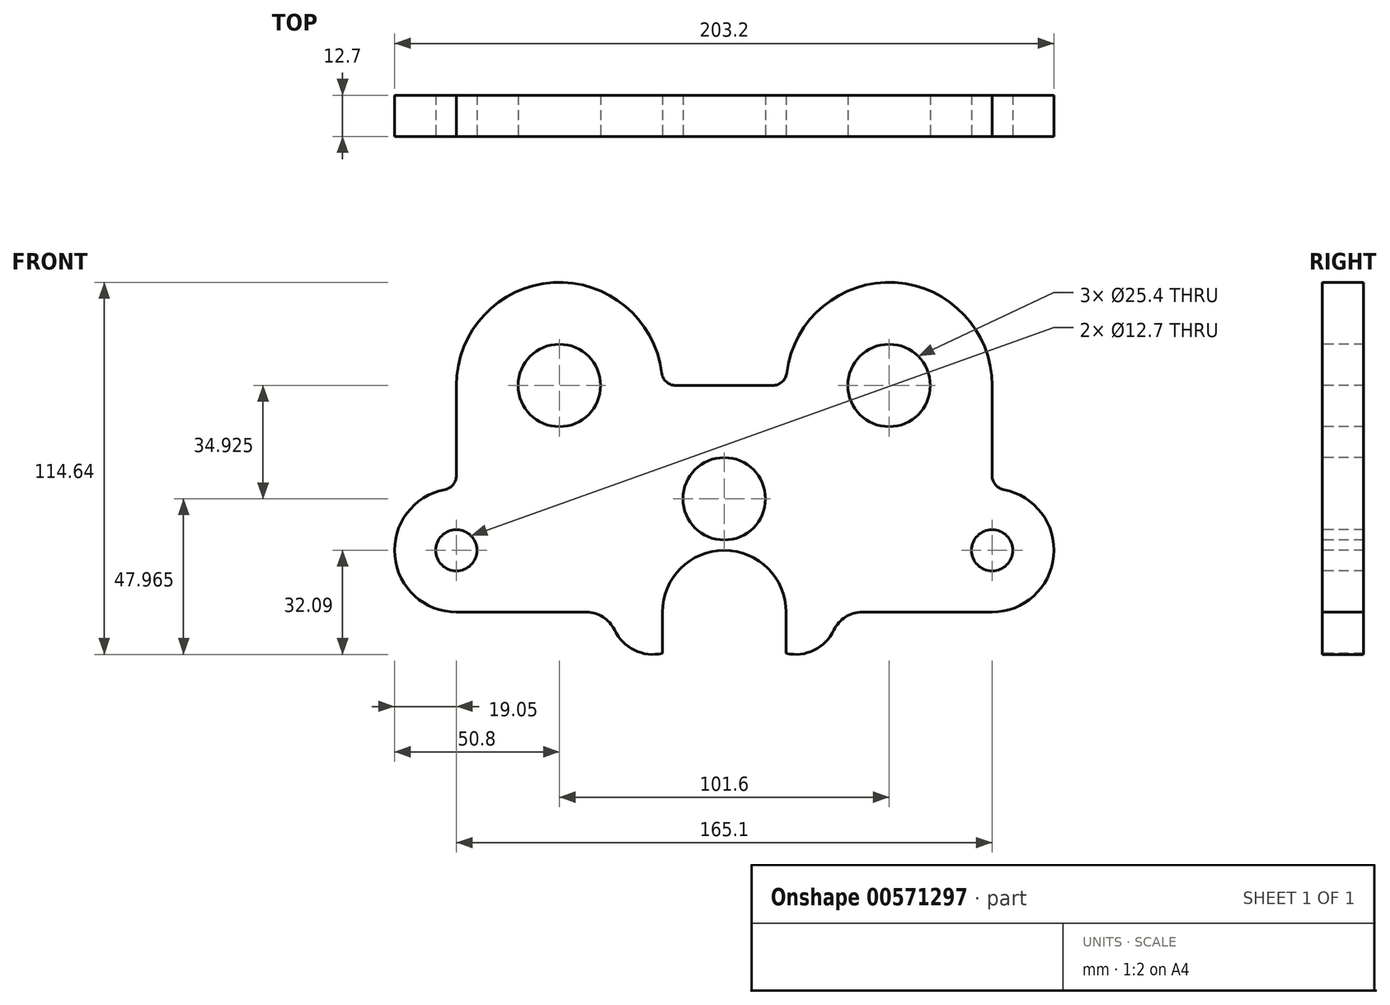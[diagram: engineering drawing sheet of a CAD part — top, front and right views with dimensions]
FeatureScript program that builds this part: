
annotation { "Feature Type Name" : "Feature", "Feature Type Description" : "" }
export const myFeature = defineFeature(function(context is Context, id is Id, definition is map)
    precondition{}
    {
        {
            var Q0;
            Q0=qCreatedBy(makeId("Front.planeOp"),FACE);
            var sketch = newSketch(context, id + "F0", { "sketchPlane" : qUnion([Q0])});
            skLineSegment(sketch, "E0", {"start": v(0, 97.1) * mm, "end": v(0, -60.42) * mm, "construction": true});
            skLineSegment(sketch, "E1", {"start": v(0, 69.85) * mm, "end": v(-14.9, 69.85) * mm});
            skArc(sketch, "E2", {"start": v(-19.29, 73.73) * mm, "mid": v(-52.74, 101.54) * mm, "end": v(-82.55, 69.85) * mm});
            skLineSegment(sketch, "E3", {"start": v(-82.55, 69.85) * mm, "end": v(-82.55, 42.1) * mm});
            skArc(sketch, "E4", {"start": v(-86.13, 37.76) * mm, "mid": v(-101.51, 17.25) * mm, "end": v(-82.55, 0) * mm});
            skLineSegment(sketch, "E5", {"start": v(-82.55, 0) * mm, "end": v(-42.46, 0) * mm});
            skArc(sketch, "E6", {"start": v(-42.46, 0) * mm, "mid": v(-37.34, -1.5) * mm, "end": v(-33.82, -5.5) * mm});
            skArc(sketch, "E7", {"start": v(-33.82, -5.5) * mm, "mid": v(-27.71, -11.72) * mm, "end": v(-19.05, -12.7) * mm});
            skLineSegment(sketch, "E8", {"start": v(-19.05, -12.7) * mm, "end": v(-19.05, 0) * mm});
            skLineSegment(sketch, "E9.MirrorCS", {"start": v(0, 69.85) * mm, "end": v(14.9, 69.85) * mm});
            skArc(sketch, "E10.MirrorCS", {"start": v(19.29, 73.73) * mm, "mid": v(52.74, 101.54) * mm, "end": v(82.55, 69.85) * mm});
            skLineSegment(sketch, "E11.MirrorCS", {"start": v(82.55, 69.85) * mm, "end": v(82.55, 42.1) * mm});
            skArc(sketch, "E12.MirrorCS", {"start": v(86.13, 37.76) * mm, "mid": v(101.51, 17.25) * mm, "end": v(82.55, 0) * mm});
            skLineSegment(sketch, "E13.MirrorCS", {"start": v(82.55, 0) * mm, "end": v(42.46, 0) * mm});
            skArc(sketch, "E14.MirrorCS", {"start": v(42.46, 0) * mm, "mid": v(37.34, -1.5) * mm, "end": v(33.82, -5.5) * mm});
            skArc(sketch, "E15.MirrorCS", {"start": v(33.82, -5.5) * mm, "mid": v(27.71, -11.72) * mm, "end": v(19.05, -12.7) * mm});
            skLineSegment(sketch, "E16.MirrorCS", {"start": v(19.05, -12.7) * mm, "end": v(19.05, 0) * mm});
            skCircle(sketch, "E17", {"center": v(50.8, 69.85) * mm, "radius": 12.7 * mm});
            skCircle(sketch, "E18", {"center": v(-82.55, 19.05) * mm, "radius": 6.35 * mm});
            skCircle(sketch, "E19", {"center": v(82.55, 19.05) * mm, "radius": 6.35 * mm});
            skCircle(sketch, "E20", {"center": v(-50.8, 69.85) * mm, "radius": 12.7 * mm});
            skArc(sketch, "E21", {"start": v(-19.05, 0) * mm, "mid": v(0, 19.05) * mm, "end": v(19.05, 0) * mm});
            skLineSegment(sketch, "E22", {"start": v(-50.8, 114.73) * mm, "end": v(-50.8, 41.14) * mm, "construction": true});
            skPoint(sketch, "E22.startSnap0", {"position": v(-50.8, 101.6) * mm});
            skLineSegment(sketch, "E23", {"start": v(-100.14, 69.85) * mm, "end": v(-29.1, 69.85) * mm, "construction": true});
            skLineSegment(sketch, "E24", {"start": v(-113.02, 19.05) * mm, "end": v(-60.7, 19.05) * mm, "construction": true});
            skPoint(sketch, "E24.endSnap0", {"position": v(-101.6, 19.05) * mm});
            skLineSegment(sketch, "E25", {"start": v(34.28, 69.85) * mm, "end": v(73, 69.85) * mm, "construction": true});
            skLineSegment(sketch, "E26", {"start": v(82.55, 33.07) * mm, "end": v(82.55, 5.84) * mm, "construction": true});
            skLineSegment(sketch, "E27", {"start": v(66.2, 19.05) * mm, "end": v(96.4, 19.05) * mm, "construction": true});
            skLineSegment(sketch, "E28", {"start": v(-23.99, 34.92) * mm, "end": v(20.1, 34.92) * mm, "construction": true});
            skCircle(sketch, "E29", {"center": v(0, 34.92) * mm, "radius": 12.7 * mm});
            skLineSegment(sketch, "E30", {"start": v(-31.9, 0) * mm, "end": v(42.46, 0) * mm, "construction": true});
            skPoint(sketch, "E31.visualSharp", {"position": v(-19.05, 69.85) * mm});
            skArc(sketch, "E31.filletArc", {"start": v(-19.29, 73.73) * mm, "mid": v(-17.83, 70.96) * mm, "end": v(-14.9, 69.85) * mm});
            skPoint(sketch, "E32.visualSharp", {"position": v(19.05, 69.85) * mm});
            skArc(sketch, "E32.filletArc", {"start": v(14.9, 69.85) * mm, "mid": v(17.83, 70.96) * mm, "end": v(19.29, 73.73) * mm});
            skPoint(sketch, "E33.visualSharp", {"position": v(-82.55, 38.1) * mm});
            skArc(sketch, "E33.filletArc", {"start": v(-86.13, 37.76) * mm, "mid": v(-83.56, 39.28) * mm, "end": v(-82.55, 42.1) * mm});
            skPoint(sketch, "E34.visualSharp", {"position": v(82.55, 38.1) * mm});
            skArc(sketch, "E34.filletArc", {"start": v(82.55, 42.1) * mm, "mid": v(83.56, 39.28) * mm, "end": v(86.13, 37.76) * mm});
            skSolve(sketch);
        }
        {
            var Q0;
            Q0 = qSketchRegion(id + "F0", true);
            extrude(context, id + "F1", {"entities" : qUnion([Q0]), "oppositeDirection" : true, "depth" : 12.7 * mm, "offsetDistance" : 25.4 * mm});
        }
    });
